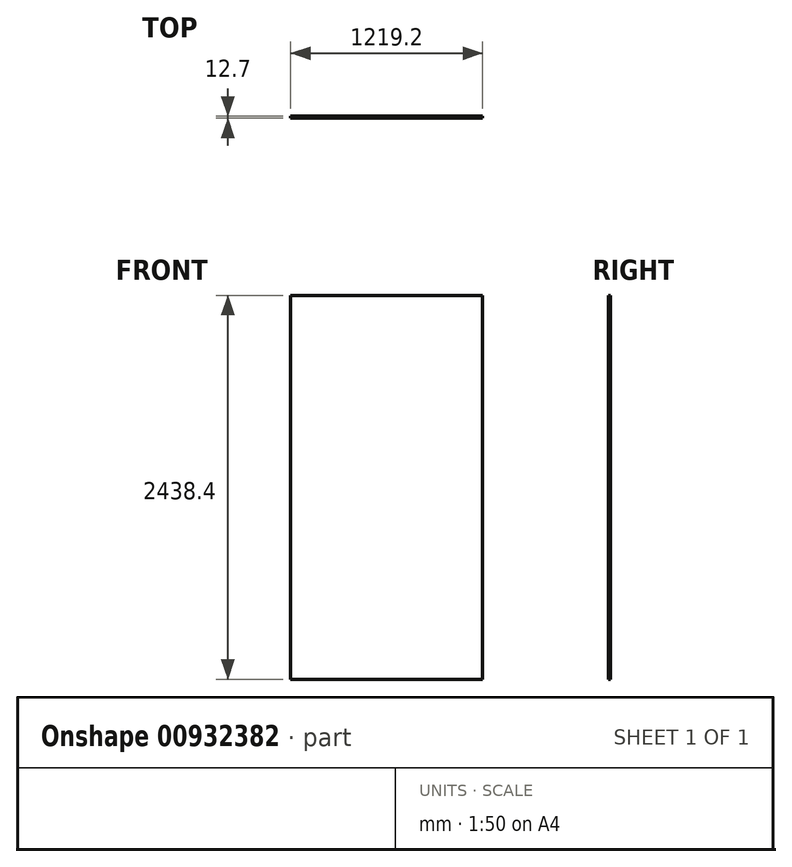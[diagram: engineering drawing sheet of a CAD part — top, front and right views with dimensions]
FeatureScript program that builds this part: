
annotation { "Feature Type Name" : "Feature", "Feature Type Description" : "" }
export const myFeature = defineFeature(function(context is Context, id is Id, definition is map)
    precondition{}
    {
        {
            var Q0;
            Q0=qCreatedBy(makeId("Front.planeOp"),FACE);
            var sketch = newSketch(context, id + "F0", { "sketchPlane" : qUnion([Q0])});
            skLineSegment(sketch, "E0.bottom", {"start": v(609.6, 1219.2) * mm, "end": v(-609.6, 1219.2) * mm});
            skLineSegment(sketch, "E0.top", {"start": v(609.6, -1219.2) * mm, "end": v(-609.6, -1219.2) * mm});
            skLineSegment(sketch, "E0.left", {"start": v(609.6, 1219.2) * mm, "end": v(609.6, -1219.2) * mm});
            skLineSegment(sketch, "E0.right", {"start": v(-609.6, 1219.2) * mm, "end": v(-609.6, -1219.2) * mm});
            skPoint(sketch, "E0.middle", {"position": v(0, 0) * mm});
            skSolve(sketch);
        }
        {
            var Q0;
            Q0=makeQuery(id+"F0.imprint","IMPRINT",FACE,{"disambiguationData":[TD([[makeQuery(id+"F0.imprint","IMPRINT",EDGE,{"derivedFrom":sQuery(id+"F0.wireOp",EDGE,"E0.bottom")}),1.0]])]});
            extrude(context, id + "F1", {"entities" : qUnion([Q0]), "depth" : 12.7 * mm, "offsetDistance" : 25.4 * mm});
        }
    });
